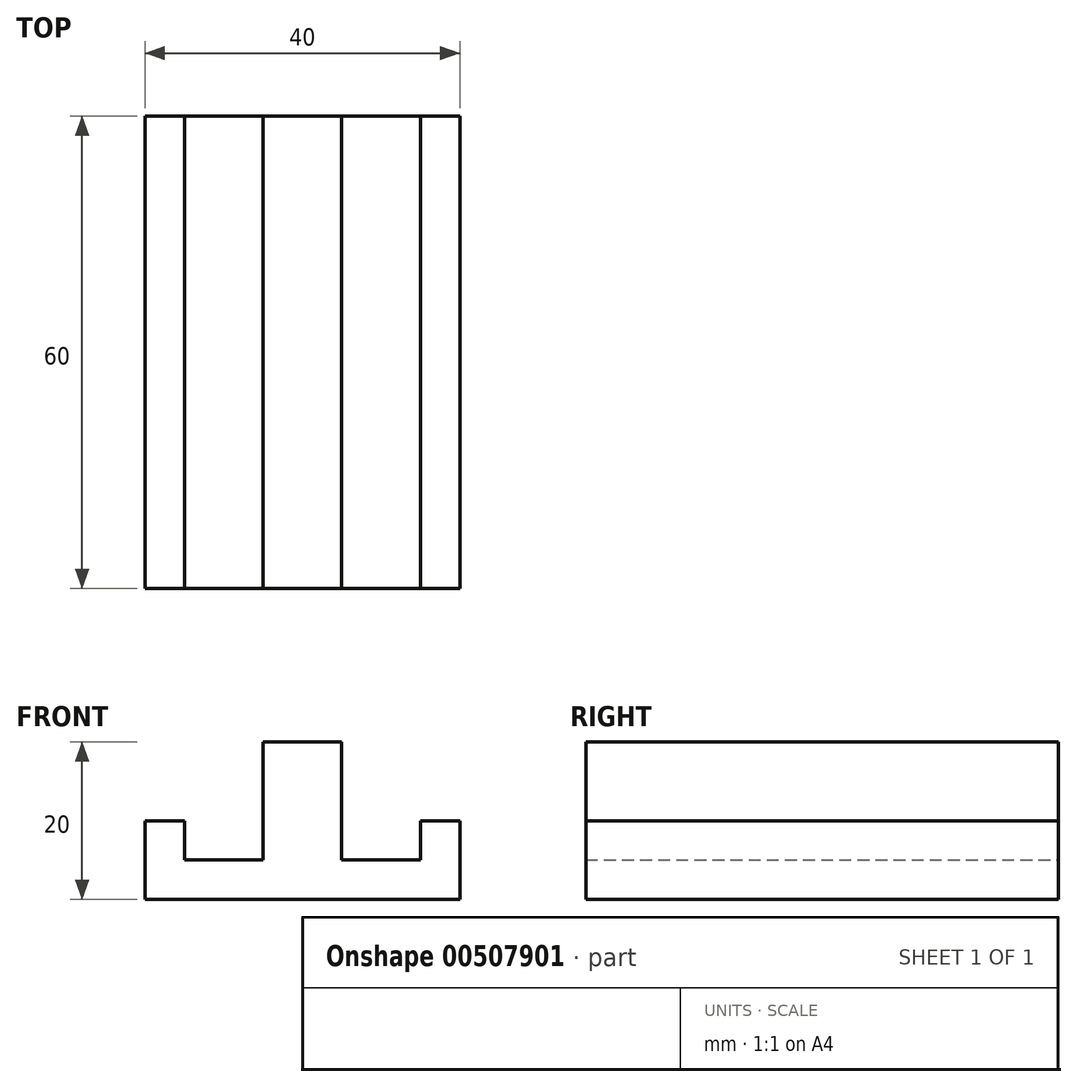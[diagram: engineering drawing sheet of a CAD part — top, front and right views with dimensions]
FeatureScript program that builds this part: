
annotation { "Feature Type Name" : "Feature", "Feature Type Description" : "" }
export const myFeature = defineFeature(function(context is Context, id is Id, definition is map)
    precondition{}
    {
        {
            var Q0;
            Q0=qCreatedBy(makeId("Front.planeOp"),FACE);
            var sketch = newSketch(context, id + "F0", { "sketchPlane" : qUnion([Q0])});
            skLineSegment(sketch, "E0", {"start": v(0, 0) * mm, "end": v(11.12, 0) * mm, "construction": true});
            skLineSegment(sketch, "E1", {"start": v(0, 0) * mm, "end": v(0, 10) * mm});
            skLineSegment(sketch, "E2", {"start": v(5, 10) * mm, "end": v(5, 5) * mm});
            skLineSegment(sketch, "E3", {"start": v(5, 5) * mm, "end": v(15, 5) * mm});
            skLineSegment(sketch, "E4", {"start": v(15, 5) * mm, "end": v(15, 20) * mm});
            skLineSegment(sketch, "E5", {"start": v(15, 20) * mm, "end": v(20, 20) * mm});
            skLineSegment(sketch, "E6", {"start": v(20, 0) * mm, "end": v(0, 0) * mm});
            skLineSegment(sketch, "E7", {"start": v(20, 0) * mm, "end": v(20, 55) * mm, "construction": true});
            skLineSegment(sketch, "E8.MirrorCS", {"start": v(25, 20) * mm, "end": v(20, 20) * mm});
            skLineSegment(sketch, "E9.MirrorCS", {"start": v(25, 5) * mm, "end": v(25, 20) * mm});
            skLineSegment(sketch, "E10.MirrorCS", {"start": v(35, 5) * mm, "end": v(25, 5) * mm});
            skLineSegment(sketch, "E11.MirrorCS", {"start": v(35, 10) * mm, "end": v(35, 5) * mm});
            skLineSegment(sketch, "E12.MirrorCS", {"start": v(40, 0) * mm, "end": v(40, 10) * mm});
            skLineSegment(sketch, "E13.MirrorCS", {"start": v(20, 0) * mm, "end": v(40, 0) * mm});
            skLineSegment(sketch, "E14", {"start": v(5, 10) * mm, "end": v(0, 10) * mm});
            skLineSegment(sketch, "E15", {"start": v(35, 10) * mm, "end": v(40, 10) * mm});
            skSolve(sketch);
        }
        {
            var Q0;
            Q0=makeQuery(id+"F0.imprint","IMPRINT",FACE,{"disambiguationData":[TD([[makeQuery(id+"F0.imprint","IMPRINT",EDGE,{"derivedFrom":sQuery(id+"F0.wireOp",EDGE,"E1")}),-1.0]])]});
            extrude(context, id + "F1", {"entities" : qUnion([Q0]), "depth" : 60 * mm, "offsetDistance" : 25 * mm, "symmetric" : true});
        }
    });
